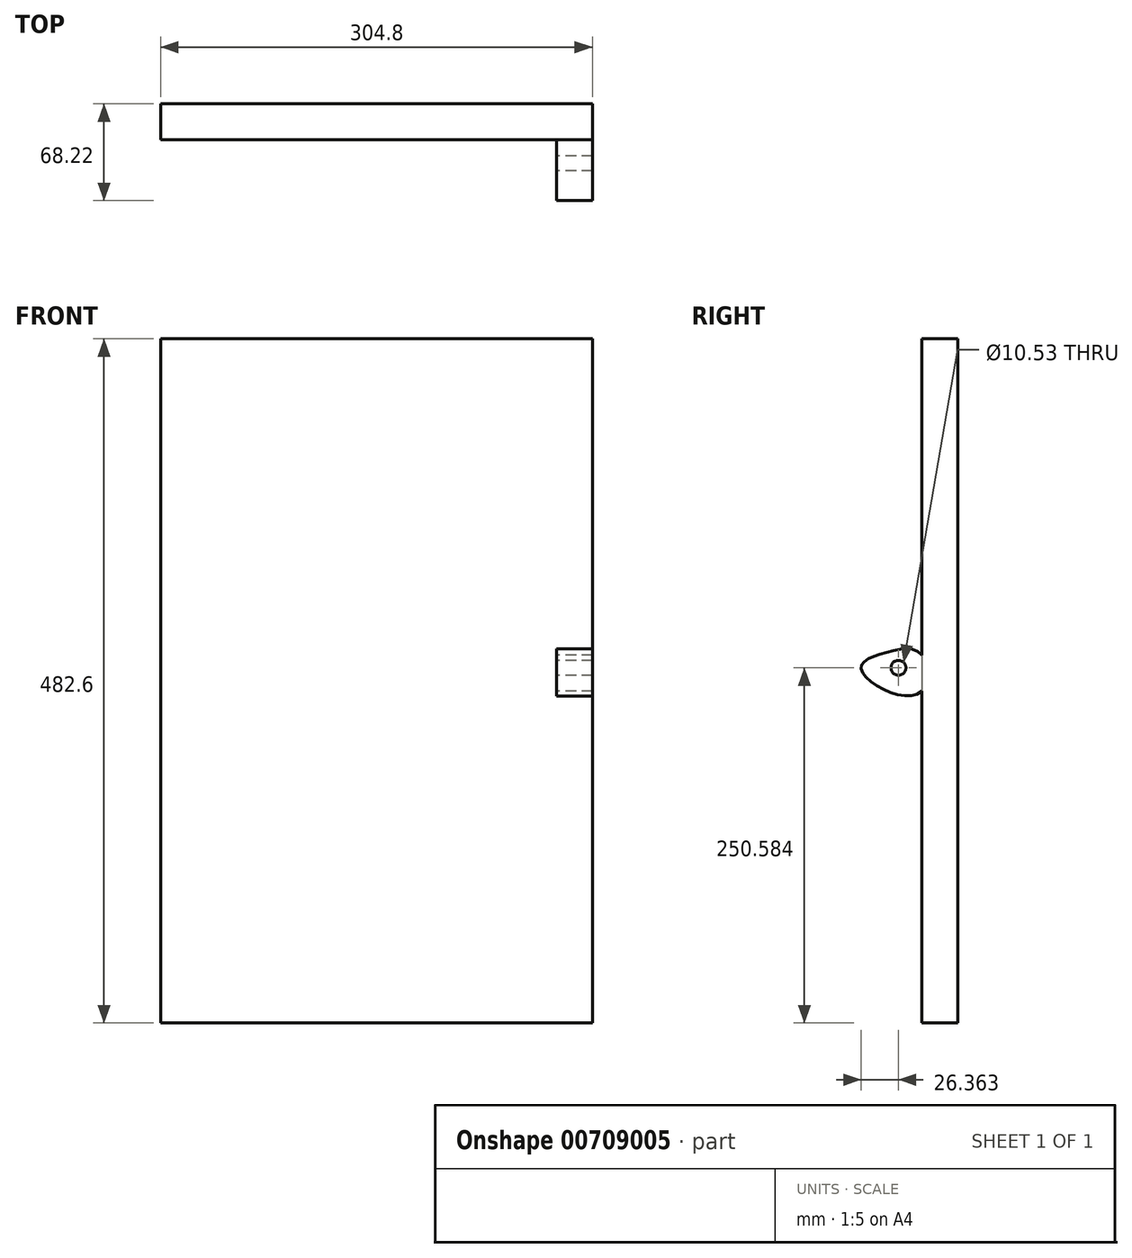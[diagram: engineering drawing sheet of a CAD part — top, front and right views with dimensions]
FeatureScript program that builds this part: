
annotation { "Feature Type Name" : "Feature", "Feature Type Description" : "" }
export const myFeature = defineFeature(function(context is Context, id is Id, definition is map)
    precondition{}
    {
        {
            var Q0;
            Q0=qCreatedBy(makeId("Front.planeOp"),FACE);
            var sketch = newSketch(context, id + "F0", { "sketchPlane" : qUnion([Q0])});
            skLineSegment(sketch, "E0.bottom", {"start": v(-139.7, 241.3) * mm, "end": v(139.7, 241.3) * mm});
            skLineSegment(sketch, "E0.top", {"start": v(-139.7, -241.3) * mm, "end": v(139.7, -241.3) * mm});
            skLineSegment(sketch, "E0.left", {"start": v(-139.7, 241.3) * mm, "end": v(-139.7, -241.3) * mm});
            skLineSegment(sketch, "E0.right", {"start": v(139.7, 241.3) * mm, "end": v(139.7, -241.3) * mm});
            skPoint(sketch, "E0.middle", {"position": v(0, 0) * mm});
            skSolve(sketch);
        }
        {
            var Q0;
            Q0=makeQuery(id+"F0.imprint","IMPRINT",FACE,{"disambiguationData":[TD([[makeQuery(id+"F0.imprint","IMPRINT",EDGE,{"derivedFrom":sQuery(id+"F0.wireOp",EDGE,"E0.bottom")}),-1.0]])]});
            extrude(context, id + "F1", {"entities" : qUnion([Q0]), "depth" : 25.4 * mm, "offsetDistance" : 25.4 * mm});
        }
        {
            var Q0;
            Q0=makeQuery(id+"F1.opExtrude","SWEPT_FACE",FACE,{"disambiguationData":[OSD([sQuery(id+"F0.wireOp",EDGE,"E0.right")])]});
            var sketch = newSketch(context, id + "F2", { "sketchPlane" : qUnion([Q0])});
            skSolve(sketch);
        }
        {
            var Q0;
            {var subQ0=sQuery(id+"F0.wireOp",EDGE,"E0.right");Q0=makeQuery(id+"F2.imprint","IMPRINT",FACE,{"disambiguationData":[TD([[makeQuery(id+"F2.imprint","IMPRINT",EDGE,{"derivedFrom":makeQuery(id+"F1.opExtrude","CAP_EDGE",EDGE,{"disambiguationData":[OSD([subQ0])],"isStart":true})}),-1.0]])]});}
            var sketch = newSketch(context, id + "F3", { "sketchPlane" : qUnion([Q0])});
            skFitSpline(sketch, "E1", {"points": [v(-26.23, 19.15) * mm, v(-50.9, 19.97) * mm, v(-68.17, 10.1) * mm, v(-51.72, -6.34) * mm, v(-24.6, -6.34) * mm, v(-26.23, 19.15) * mm]});
            skCircle(sketch, "E2", {"center": v(-41.86, 9.28) * mm, "radius": 5.26 * mm});
            skSolve(sketch);
        }
        {
            var Q0;
            Q0=makeQuery(id+"F3.imprint","IMPRINT",FACE,{"disambiguationData":[TD([[makeQuery(id+"F3.imprint","IMPRINT",EDGE,{"derivedFrom":sQuery(id+"F3.wireOp",EDGE,"E2")}),-1.0]])]});
            var Q1;
            {var subQ0=sQuery(id+"F0.wireOp",EDGE,"E0.right");Q1=makeQuery(id+"F2.imprint","IMPRINT",FACE,{"disambiguationData":[TD([[makeQuery(id+"F2.imprint","IMPRINT",EDGE,{"derivedFrom":makeQuery(id+"F1.opExtrude","CAP_EDGE",EDGE,{"disambiguationData":[OSD([subQ0])],"isStart":true})}),-1.0]])]});}
            extrude(context, id + "F4", {"entities" : qUnion([Q0, Q1]), "operationType" : NewBodyOperationType.ADD, "depth" : 25.4 * mm, "offsetDistance" : 25.4 * mm});
        }
    });
